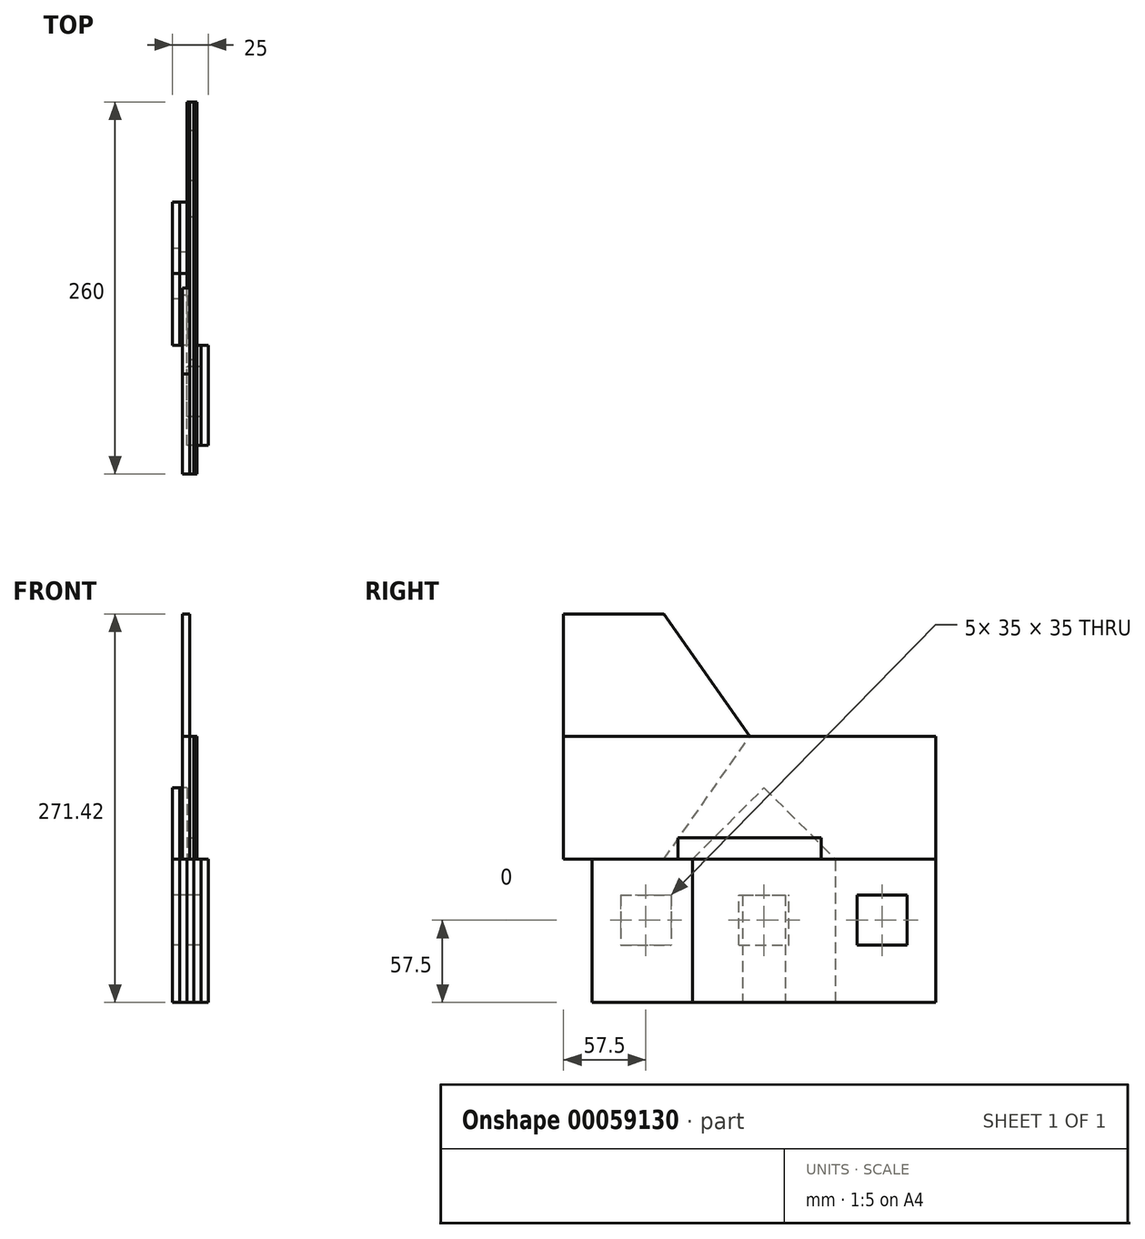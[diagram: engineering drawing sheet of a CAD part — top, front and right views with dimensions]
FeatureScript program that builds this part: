
annotation { "Feature Type Name" : "Feature", "Feature Type Description" : "" }
export const myFeature = defineFeature(function(context is Context, id is Id, definition is map)
    precondition{}
    {
        {
            var Q0;
            Q0=qCreatedBy(makeId("Right.planeOp"),FACE);
            var sketch = newSketch(context, id + "F0", { "sketchPlane" : qUnion([Q0])});
            skLineSegment(sketch, "E0.bottom", {"start": v(0, 0) * mm, "end": v(-100, 0) * mm});
            skLineSegment(sketch, "E0.top", {"start": v(0, 100) * mm, "end": v(-100, 100) * mm});
            skLineSegment(sketch, "E0.left", {"start": v(0, 0) * mm, "end": v(0, 100) * mm});
            skLineSegment(sketch, "E0.right", {"start": v(-100, 0) * mm, "end": v(-100, 100) * mm});
            skLineSegment(sketch, "E1", {"start": v(-100, 100) * mm, "end": v(-50, 150) * mm});
            skLineSegment(sketch, "E2", {"start": v(-50, 150) * mm, "end": v(0, 100) * mm});
            skLineSegment(sketch, "E3.bottom", {"start": v(-67.5, 40) * mm, "end": v(-32.5, 40) * mm});
            skLineSegment(sketch, "E3.top", {"start": v(-67.5, 75) * mm, "end": v(-32.5, 75) * mm});
            skLineSegment(sketch, "E3.left", {"start": v(-67.5, 40) * mm, "end": v(-67.5, 75) * mm});
            skLineSegment(sketch, "E3.right", {"start": v(-32.5, 40) * mm, "end": v(-32.5, 75) * mm});
            skSolve(sketch);
        }
        {
            var Q0;
            Q0 = qSketchRegion(id + "F0", true);
            extrude(context, id + "F1", {"entities" : qUnion([Q0]), "depth" : 5 * mm});
        }
        {
            var Q0;
            Q0=makeQuery(id+"F1.opExtrude","CAP_FACE",FACE,{"disambiguationData":[OSD([sQuery(id+"F0.wireOp",EDGE,"E0.bottom"),sQuery(id+"F0.wireOp",EDGE,"E0.left"),sQuery(id+"F0.wireOp",EDGE,"E0.right"),sQuery(id+"F0.wireOp",EDGE,"E1"),sQuery(id+"F0.wireOp",EDGE,"E2"),sQuery(id+"F0.wireOp",EDGE,"E3.bottom"),sQuery(id+"F0.wireOp",EDGE,"E3.top"),sQuery(id+"F0.wireOp",EDGE,"E3.left"),sQuery(id+"F0.wireOp",EDGE,"E3.right")])],"isStart":false});
            var sketch = newSketch(context, id + "F2", { "sketchPlane" : qUnion([Q0])});
            skLineSegment(sketch, "E4", {"start": v(-100, 0) * mm, "end": v(-100, 100) * mm});
            skLineSegment(sketch, "E5", {"start": v(-100, 100) * mm, "end": v(-50, 150) * mm});
            skLineSegment(sketch, "E6", {"start": v(-50, 150) * mm, "end": v(0, 100) * mm});
            skLineSegment(sketch, "E7", {"start": v(0, 100) * mm, "end": v(0, 0) * mm});
            skLineSegment(sketch, "E8", {"start": v(0, 0) * mm, "end": v(-100, 0) * mm});
            skLineSegment(sketch, "E9.bottom", {"start": v(-65, 75) * mm, "end": v(-35, 75) * mm});
            skLineSegment(sketch, "E9.top", {"start": v(-65, 0) * mm, "end": v(-35, 0) * mm});
            skLineSegment(sketch, "E9.left", {"start": v(-65, 75) * mm, "end": v(-65, 0) * mm});
            skLineSegment(sketch, "E9.right", {"start": v(-35, 75) * mm, "end": v(-35, 0) * mm});
            skSolve(sketch);
        }
        {
            var Q0;
            {var subQ8=sQuery(id+"F2.wireOp",EDGE,"E4");Q0=makeQuery(id+"F2.imprint","IMPRINT",FACE,{"disambiguationData":[TD([[makeQuery(id+"F2.imprint","IMPRINT",EDGE,{"derivedFrom":subQ8}),-1.0]])]});}
            var Q1;
            {var subQ5=makeQuery(id+"F1.opExtrude","CAP_EDGE",EDGE,{"disambiguationData":[OSD([sQuery(id+"F0.wireOp",EDGE,"E3.left")])],"isStart":false});Q1=makeQuery(id+"F2.imprint","IMPRINT",FACE,{"disambiguationData":[TD([[makeQuery(id+"F2.imprint","IMPRINT",EDGE,{"derivedFrom":subQ5}),-1.0]])]});}
            var Q2;
            {var subQ5=makeQuery(id+"F1.opExtrude","CAP_EDGE",EDGE,{"disambiguationData":[OSD([sQuery(id+"F0.wireOp",EDGE,"E3.right")])],"isStart":false});Q2=makeQuery(id+"F2.imprint","IMPRINT",FACE,{"disambiguationData":[TD([[makeQuery(id+"F2.imprint","IMPRINT",EDGE,{"derivedFrom":subQ5}),1.0]])]});}
            extrude(context, id + "F3", {"entities" : qUnion([Q0, Q1, Q2]), "depth" : 5 * mm});
        }
        {
            var Q0;
            Q0 = qSketchRegion(id + "F0", true);
            extrude(context, id + "F4", {"entities" : qUnion([Q0]), "depth" : 5 * mm});
        }
        {
            var Q0;
            Q0=makeQuery(id+"F3.opExtrude","CAP_FACE",FACE,{"disambiguationData":[OSD([sQuery(id+"F2.wireOp",EDGE,"E4"),sQuery(id+"F2.wireOp",EDGE,"E5"),sQuery(id+"F2.wireOp",EDGE,"E6"),sQuery(id+"F2.wireOp",EDGE,"E7"),sQuery(id+"F2.wireOp",EDGE,"E8"),sQuery(id+"F2.wireOp",EDGE,"E9.bottom"),sQuery(id+"F2.wireOp",EDGE,"E9.left"),sQuery(id+"F2.wireOp",EDGE,"E9.right")])],"isStart":false});
            var sketch = newSketch(context, id + "F5", { "sketchPlane" : qUnion([Q0])});
            skLineSegment(sketch, "E10.bottom", {"start": v(-170, 0) * mm, "end": v(70, 0) * mm});
            skLineSegment(sketch, "E10.top", {"start": v(-170, 100) * mm, "end": v(70, 100) * mm});
            skLineSegment(sketch, "E10.left", {"start": v(-170, 0) * mm, "end": v(-170, 100) * mm});
            skLineSegment(sketch, "E10.right", {"start": v(70, 0) * mm, "end": v(70, 100) * mm});
            skLineSegment(sketch, "E11.bottom", {"start": v(-150, 75) * mm, "end": v(-115, 75) * mm});
            skLineSegment(sketch, "E11.top", {"start": v(-150, 40) * mm, "end": v(-115, 40) * mm});
            skLineSegment(sketch, "E11.left", {"start": v(-150, 75) * mm, "end": v(-150, 40) * mm});
            skLineSegment(sketch, "E11.right", {"start": v(-115, 75) * mm, "end": v(-115, 40) * mm});
            skLineSegment(sketch, "E12.bottom", {"start": v(15, 75) * mm, "end": v(50, 75) * mm});
            skLineSegment(sketch, "E12.top", {"start": v(15, 40) * mm, "end": v(50, 40) * mm});
            skLineSegment(sketch, "E12.left", {"start": v(15, 75) * mm, "end": v(15, 40) * mm});
            skLineSegment(sketch, "E12.right", {"start": v(50, 75) * mm, "end": v(50, 40) * mm});
            skSolve(sketch);
        }
        {
            var Q0;
            Q0 = qSketchRegion(id + "F5", true);
            extrude(context, id + "F6", {"entities" : qUnion([Q0]), "depth" : 5 * mm});
        }
        {
            var Q0;
            Q0=makeQuery(id+"F6.opExtrude","CAP_FACE",FACE,{"disambiguationData":[OSD([sQuery(id+"F5.wireOp",EDGE,"E10.bottom"),sQuery(id+"F5.wireOp",EDGE,"E10.top"),sQuery(id+"F5.wireOp",EDGE,"E10.left"),sQuery(id+"F5.wireOp",EDGE,"E10.right"),sQuery(id+"F5.wireOp",EDGE,"E11.bottom"),sQuery(id+"F5.wireOp",EDGE,"E11.top"),sQuery(id+"F5.wireOp",EDGE,"E11.left"),sQuery(id+"F5.wireOp",EDGE,"E11.right"),sQuery(id+"F5.wireOp",EDGE,"E12.bottom"),sQuery(id+"F5.wireOp",EDGE,"E12.top"),sQuery(id+"F5.wireOp",EDGE,"E12.left"),sQuery(id+"F5.wireOp",EDGE,"E12.right")])],"isStart":false});
            var sketch = newSketch(context, id + "F7", { "sketchPlane" : qUnion([Q0])});
            skLineSegment(sketch, "E13.bottom", {"start": v(-170, 0) * mm, "end": v(-100, 0) * mm});
            skLineSegment(sketch, "E13.top", {"start": v(-170, 100) * mm, "end": v(-100, 100) * mm});
            skLineSegment(sketch, "E13.left", {"start": v(-170, 0) * mm, "end": v(-170, 100) * mm});
            skLineSegment(sketch, "E13.right", {"start": v(-100, 0) * mm, "end": v(-100, 100) * mm});
            skLineSegment(sketch, "E14.bottom", {"start": v(-150, 75) * mm, "end": v(-115, 75) * mm});
            skLineSegment(sketch, "E14.top", {"start": v(-150, 40) * mm, "end": v(-115, 40) * mm});
            skLineSegment(sketch, "E14.left", {"start": v(-150, 75) * mm, "end": v(-150, 40) * mm});
            skLineSegment(sketch, "E14.right", {"start": v(-115, 75) * mm, "end": v(-115, 40) * mm});
            skSolve(sketch);
        }
        {
            var Q0;
            Q0 = qSketchRegion(id + "F7", true);
            extrude(context, id + "F8", {"entities" : qUnion([Q0]), "depth" : 5 * mm});
        }
        {
            var Q0;
            Q0=makeQuery(id+"F8.opExtrude","CAP_FACE",FACE,{"disambiguationData":[OSD([sQuery(id+"F7.wireOp",EDGE,"E13.bottom"),sQuery(id+"F7.wireOp",EDGE,"E13.top"),sQuery(id+"F7.wireOp",EDGE,"E13.left"),sQuery(id+"F7.wireOp",EDGE,"E13.right"),sQuery(id+"F7.wireOp",EDGE,"E14.bottom"),sQuery(id+"F7.wireOp",EDGE,"E14.top"),sQuery(id+"F7.wireOp",EDGE,"E14.left"),sQuery(id+"F7.wireOp",EDGE,"E14.right")])],"isStart":false});
            var sketch = newSketch(context, id + "F9", { "sketchPlane" : qUnion([Q0])});
            skLineSegment(sketch, "E15.bottom", {"start": v(-170, 100) * mm, "end": v(-100, 100) * mm});
            skLineSegment(sketch, "E15.top", {"start": v(-170, 0) * mm, "end": v(-100, 0) * mm});
            skLineSegment(sketch, "E15.left", {"start": v(-170, 100) * mm, "end": v(-170, 0) * mm});
            skLineSegment(sketch, "E15.right", {"start": v(-100, 100) * mm, "end": v(-100, 0) * mm});
            skSolve(sketch);
        }
        {
            var Q0;
            Q0 = qSketchRegion(id + "F9", true);
            extrude(context, id + "F10", {"entities" : qUnion([Q0]), "depth" : 5 * mm});
        }
        {
            var Q0;
            Q0=makeQuery(id+"F6.opExtrude","CAP_FACE",FACE,{"disambiguationData":[OSD([sQuery(id+"F5.wireOp",EDGE,"E10.bottom"),sQuery(id+"F5.wireOp",EDGE,"E10.top"),sQuery(id+"F5.wireOp",EDGE,"E10.left"),sQuery(id+"F5.wireOp",EDGE,"E10.right"),sQuery(id+"F5.wireOp",EDGE,"E11.bottom"),sQuery(id+"F5.wireOp",EDGE,"E11.top"),sQuery(id+"F5.wireOp",EDGE,"E11.left"),sQuery(id+"F5.wireOp",EDGE,"E11.right"),sQuery(id+"F5.wireOp",EDGE,"E12.bottom"),sQuery(id+"F5.wireOp",EDGE,"E12.top"),sQuery(id+"F5.wireOp",EDGE,"E12.left"),sQuery(id+"F5.wireOp",EDGE,"E12.right")])],"isStart":false});
            var sketch = newSketch(context, id + "F11", { "sketchPlane" : qUnion([Q0])});
            skLineSegment(sketch, "E16.bottom", {"start": v(70, 100) * mm, "end": v(-190, 100) * mm});
            skLineSegment(sketch, "E16.top", {"start": v(70, 185.71) * mm, "end": v(-190, 185.71) * mm});
            skLineSegment(sketch, "E16.left", {"start": v(70, 100) * mm, "end": v(70, 185.71) * mm});
            skLineSegment(sketch, "E16.right", {"start": v(-190, 100) * mm, "end": v(-190, 185.71) * mm});
            skSolve(sketch);
        }
        {
            var Q0;
            Q0 = qSketchRegion(id + "F11", true);
            extrude(context, id + "F12", {"entities" : qUnion([Q0]), "depth" : 2 * mm});
        }
        {
            var Q0;
            Q0=makeQuery(id+"F12.opExtrude","CAP_FACE",FACE,{"disambiguationData":[OSD([sQuery(id+"F11.wireOp",EDGE,"E16.bottom"),sQuery(id+"F11.wireOp",EDGE,"E16.top"),sQuery(id+"F11.wireOp",EDGE,"E16.left"),sQuery(id+"F11.wireOp",EDGE,"E16.right")])],"isStart":false});
            var sketch = newSketch(context, id + "F13", { "sketchPlane" : qUnion([Q0])});
            skLineSegment(sketch, "E17.bottom", {"start": v(-190, 185.71) * mm, "end": v(70, 185.71) * mm});
            skLineSegment(sketch, "E17.top", {"start": v(-190, 100) * mm, "end": v(70, 100) * mm});
            skLineSegment(sketch, "E17.left", {"start": v(-190, 185.71) * mm, "end": v(-190, 100) * mm});
            skLineSegment(sketch, "E17.right", {"start": v(70, 185.71) * mm, "end": v(70, 100) * mm});
            skLineSegment(sketch, "E18.bottom", {"start": v(-110, 100) * mm, "end": v(-10, 100) * mm});
            skLineSegment(sketch, "E18.top", {"start": v(-110, 115) * mm, "end": v(-10, 115) * mm});
            skLineSegment(sketch, "E18.left", {"start": v(-110, 100) * mm, "end": v(-110, 115) * mm});
            skLineSegment(sketch, "E18.right", {"start": v(-10, 100) * mm, "end": v(-10, 115) * mm});
            skSolve(sketch);
        }
        {
            var Q0;
            Q0=makeQuery(id+"F13.imprint","IMPRINT",FACE,{"disambiguationData":[TD([[makeQuery(id+"F13.imprint","IMPRINT",EDGE,{"derivedFrom":sQuery(id+"F13.wireOp",EDGE,"E17.bottom")}),1.0]])]});
            extrude(context, id + "F14", {"entities" : qUnion([Q0]), "oppositeDirection" : true, "depth" : 5 * mm});
        }
        {
            var Q0;
            Q0=makeQuery(id+"F14.opExtrude","CAP_FACE",FACE,{"disambiguationData":[OSD([sQuery(id+"F13.wireOp",EDGE,"E17.bottom"),sQuery(id+"F13.wireOp",EDGE,"E17.top"),sQuery(id+"F13.wireOp",EDGE,"E17.left"),sQuery(id+"F13.wireOp",EDGE,"E17.right"),sQuery(id+"F13.wireOp",EDGE,"E18.top"),sQuery(id+"F13.wireOp",EDGE,"E18.left"),sQuery(id+"F13.wireOp",EDGE,"E18.right")])],"isStart":false});
            var sketch = newSketch(context, id + "F15", { "sketchPlane" : qUnion([Q0])});
            skLineSegment(sketch, "E19.bottom", {"start": v(190, 185.71) * mm, "end": v(120, 185.71) * mm});
            skLineSegment(sketch, "E19.top", {"start": v(190, 100) * mm, "end": v(120, 100) * mm});
            skLineSegment(sketch, "E19.left", {"start": v(190, 185.71) * mm, "end": v(190, 100) * mm});
            skLineSegment(sketch, "E19.right", {"start": v(120, 185.71) * mm, "end": v(120, 100) * mm});
            skLineSegment(sketch, "E20", {"start": v(120, 100) * mm, "end": v(60, 185.71) * mm});
            skLineSegment(sketch, "E21", {"start": v(60, 185.71) * mm, "end": v(120, 185.71) * mm});
            skSolve(sketch);
        }
        {
            var Q0;
            Q0 = qSketchRegion(id + "F15", true);
            extrude(context, id + "F16", {"entities" : qUnion([Q0]), "depth" : 5 * mm});
        }
        {
            var Q0;
            Q0=makeQuery(id+"F16.opExtrude","SWEPT_BODY",BODY,{"disambiguationData":[OSD([sQuery(id+"F15.wireOp",EDGE,"E19.bottom"),sQuery(id+"F15.wireOp",EDGE,"E19.top"),sQuery(id+"F15.wireOp",EDGE,"E19.left"),sQuery(id+"F15.wireOp",EDGE,"E20"),sQuery(id+"F15.wireOp",EDGE,"E21")])]});
            var Q1;
            Q1=makeQuery(id+"F16.opExtrude","SWEPT_FACE",FACE,{"disambiguationData":[OSD([sQuery(id+"F15.wireOp",EDGE,"E19.bottom"),sQuery(id+"F15.wireOp",EDGE,"E21")])]});
            mirror(context, id + "F17", {"entities" : qUnion([Q0]), "mirrorPlane" : qUnion([Q1])});
        }
    });
